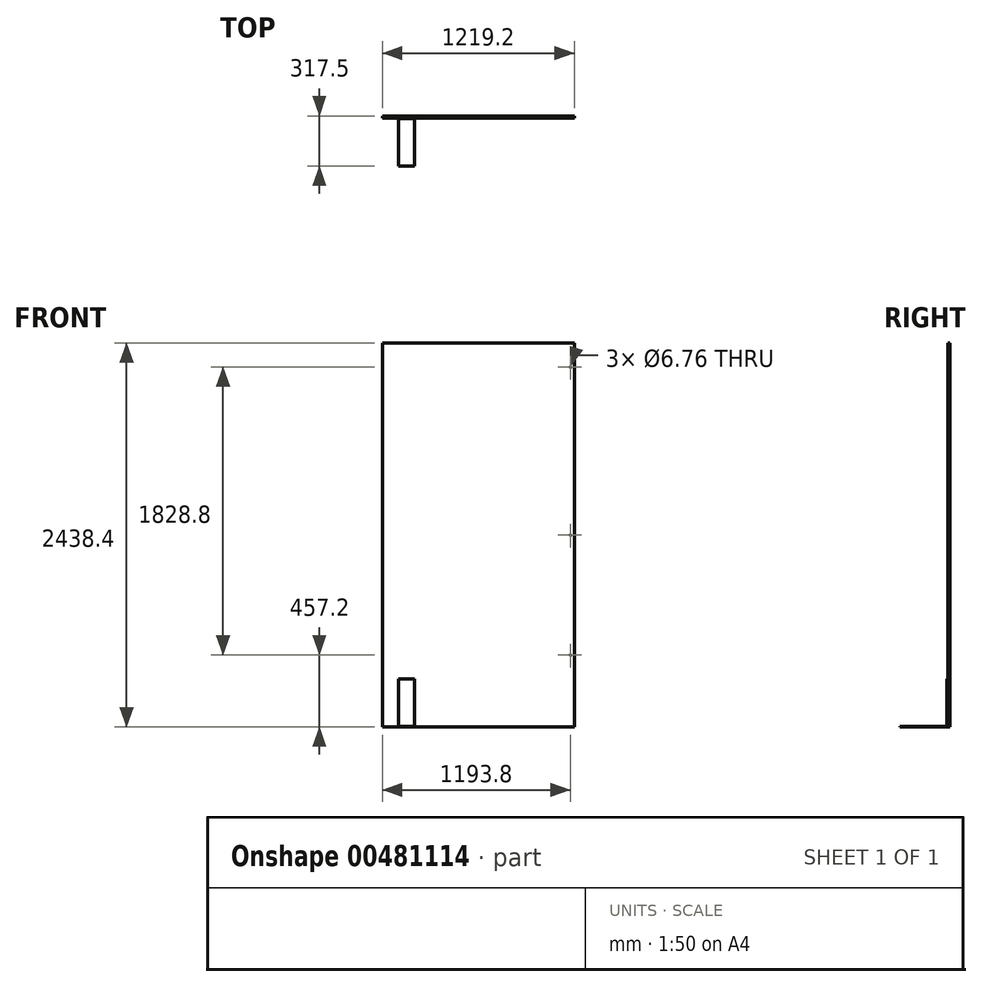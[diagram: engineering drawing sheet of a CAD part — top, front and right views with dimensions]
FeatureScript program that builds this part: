
annotation { "Feature Type Name" : "Feature", "Feature Type Description" : "" }
export const myFeature = defineFeature(function(context is Context, id is Id, definition is map)
    precondition{}
    {
        {
            var Q0;
            Q0=qCreatedBy(makeId("Front.planeOp"),FACE);
            var sketch = newSketch(context, id + "F0", { "sketchPlane" : qUnion([Q0])});
            skLineSegment(sketch, "E0.bottom", {"start": v(609.6, -1219.2) * mm, "end": v(-609.6, -1219.2) * mm});
            skLineSegment(sketch, "E0.top", {"start": v(609.6, 1219.2) * mm, "end": v(-609.6, 1219.2) * mm});
            skLineSegment(sketch, "E0.left", {"start": v(609.6, -1219.2) * mm, "end": v(609.6, 1219.2) * mm});
            skLineSegment(sketch, "E0.right", {"start": v(-609.6, -1219.2) * mm, "end": v(-609.6, 1219.2) * mm});
            skPoint(sketch, "E0.middle", {"position": v(0, 0) * mm});
            skSolve(sketch);
        }
        {
            var Q0;
            Q0 = qSketchRegion(id + "F0", true);
            extrude(context, id + "F1", {"entities" : qUnion([Q0]), "depth" : 12.7 * mm});
        }
        {
            var Q0;
            Q0=makeQuery(id+"F1.opExtrude","CAP_FACE",FACE,{"disambiguationData":[OSD([sQuery(id+"F0.wireOp",EDGE,"E0.bottom"),sQuery(id+"F0.wireOp",EDGE,"E0.top"),sQuery(id+"F0.wireOp",EDGE,"E0.left"),sQuery(id+"F0.wireOp",EDGE,"E0.right")])],"isStart":false});
            var sketch = newSketch(context, id + "F2", { "sketchPlane" : qUnion([Q0])});
            skLineSegment(sketch, "E1.bottom", {"start": v(-508, -1219.2) * mm, "end": v(-406.4, -1219.2) * mm});
            skLineSegment(sketch, "E1.top", {"start": v(-508, -914.4) * mm, "end": v(-406.4, -914.4) * mm});
            skLineSegment(sketch, "E1.left", {"start": v(-508, -1219.2) * mm, "end": v(-508, -914.4) * mm});
            skLineSegment(sketch, "E1.right", {"start": v(-406.4, -1219.2) * mm, "end": v(-406.4, -914.4) * mm});
            skLineSegment(sketch, "E2", {"start": v(0, 1219.2) * mm, "end": v(0, -1219.2) * mm, "construction": true});
            skSolve(sketch);
        }
        {
            var Q0;
            Q0=makeQuery(id+"F2.imprint","IMPRINT",FACE,{"disambiguationData":[TD([[makeQuery(id+"F2.imprint","IMPRINT",EDGE,{"derivedFrom":sQuery(id+"F2.wireOp",EDGE,"E1.bottom")}),-1.0]])]});
            extrude(context, id + "F3", {"entities" : qUnion([Q0]), "operationType" : NewBodyOperationType.ADD, "depth" : 4.83 * mm});
        }
        {
            var Q0;
            Q0=makeQuery(id+"F3.opExtrude","SWEPT_FACE",FACE,{"disambiguationData":[OSD([sQuery(id+"F2.wireOp",EDGE,"E1.left")])]});
            var sketch = newSketch(context, id + "F4", { "sketchPlane" : qUnion([Q0])});
            skLineSegment(sketch, "E3.bottom", {"start": v(12.7, -1219.2) * mm, "end": v(317.5, -1219.2) * mm});
            skLineSegment(sketch, "E3.top", {"start": v(12.7, -1214.37) * mm, "end": v(317.5, -1214.37) * mm});
            skLineSegment(sketch, "E3.left", {"start": v(12.7, -1219.2) * mm, "end": v(12.7, -1214.37) * mm});
            skLineSegment(sketch, "E3.right", {"start": v(317.5, -1219.2) * mm, "end": v(317.5, -1214.37) * mm});
            skSolve(sketch);
        }
        {
            var Q0;
            Q0 = qSketchRegion(id + "F4", true);
            extrude(context, id + "F5", {"entities" : qUnion([Q0]), "operationType" : NewBodyOperationType.ADD, "oppositeDirection" : true, "depth" : 101.6 * mm});
        }
        {
            var Q0;
            Q0=makeQuery(id+"F1.opExtrude","CAP_FACE",FACE,{"disambiguationData":[OSD([sQuery(id+"F0.wireOp",EDGE,"E0.bottom"),sQuery(id+"F0.wireOp",EDGE,"E0.top"),sQuery(id+"F0.wireOp",EDGE,"E0.left"),sQuery(id+"F0.wireOp",EDGE,"E0.right")])],"isStart":true});
            var Q1;
            Q1=makeQuery(id+"F1.opExtrude","CAP_FACE",FACE,{"disambiguationData":[OSD([sQuery(id+"F0.wireOp",EDGE,"E0.bottom"),sQuery(id+"F0.wireOp",EDGE,"E0.top"),sQuery(id+"F0.wireOp",EDGE,"E0.left"),sQuery(id+"F0.wireOp",EDGE,"E0.right")])],"isStart":false});
            cPlane(context, id + "F6", {"entities" : qUnion([Q0, Q1]), "cplaneType" : CPlaneType.MID_PLANE, "offset" : 25.4 * mm, "width" : 152.4 * mm, "height" : 152.4 * mm});
        }
        {
            var Q0;
            Q0=makeQuery(id+"F1.opExtrude","CAP_FACE",FACE,{"disambiguationData":[OSD([sQuery(id+"F0.wireOp",EDGE,"E0.bottom"),sQuery(id+"F0.wireOp",EDGE,"E0.top"),sQuery(id+"F0.wireOp",EDGE,"E0.left"),sQuery(id+"F0.wireOp",EDGE,"E0.right")])],"isStart":true});
            var sketch = newSketch(context, id + "F7", { "sketchPlane" : qUnion([Q0])});
            skLineSegment(sketch, "E4", {"start": v(-584.2, 1219.2) * mm, "end": v(-584.2, -1219.2) * mm, "construction": true});
            skCircle(sketch, "E5", {"center": v(-584.2, 1066.8) * mm, "radius": 3.38 * mm});
            skCircle(sketch, "E6", {"center": v(-584.2, 0) * mm, "radius": 3.38 * mm});
            skCircle(sketch, "E7", {"center": v(-584.2, -762) * mm, "radius": 3.38 * mm});
            skSolve(sketch);
        }
        {
            var Q0;
            Q0=makeQuery(id+"F7.imprint","IMPRINT",FACE,{"disambiguationData":[TD([[makeQuery(id+"F7.imprint","IMPRINT",EDGE,{"derivedFrom":sQuery(id+"F7.wireOp",EDGE,"E5")}),1.0]])]});
            var Q1;
            Q1=makeQuery(id+"F7.imprint","IMPRINT",FACE,{"disambiguationData":[TD([[makeQuery(id+"F7.imprint","IMPRINT",EDGE,{"derivedFrom":sQuery(id+"F7.wireOp",EDGE,"E7")}),1.0]])]});
            var Q2;
            Q2=makeQuery(id+"F7.imprint","IMPRINT",FACE,{"disambiguationData":[TD([[makeQuery(id+"F7.imprint","IMPRINT",EDGE,{"derivedFrom":sQuery(id+"F7.wireOp",EDGE,"E6")}),1.0]])]});
            var Q3;
            Q3=sQuery(id+"F7.wireOp",EDGE,"E5");
            var Q4;
            Q4=sQuery(id+"F7.wireOp",EDGE,"E7");
            var Q5;
            Q5=sQuery(id+"F7.wireOp",EDGE,"E6");
            extrude(context, id + "F8", {"entities" : qUnion([Q0, Q1, Q2]), "operationType" : NewBodyOperationType.REMOVE, "surfaceEntities" : qUnion([Q3, Q4, Q5]), "endBound" : BoundingType.THROUGH_ALL, "oppositeDirection" : true, "depth" : 25.4 * mm});
        }
    });
